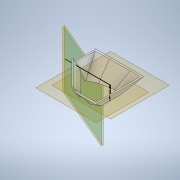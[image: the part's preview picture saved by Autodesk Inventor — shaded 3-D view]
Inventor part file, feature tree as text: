
AUTODESK INVENTOR PART (.ipt)
format: ipt  version: 2022 (Build 260153000, 153)  size: 218,112 bytes
history: native  units: in
note: dims shown in document units (in); Inventor stores cm internally (conversion verified against a paired STEP export)
features: plane x6, sketch x5, loft x1, shell x1, extrude x1, split x1
ambient origin geometry x8: Origin, YZ Plane, XZ Plane, XY Plane, X Axis, Y Axis, Z Axis, Center Point
bodies: Solid1 (feature_tree)
feature tree (15):
  sketch  "Sketch1"  dims[d0=0.1378in d1=0.2756in d2=0.1181in]
  sketch  "Sketch2"  dims[d3=120.0deg d4=0.962in]
  plane  "Work Plane8"
  plane  "Work Plane7"
  plane  "Work Plane9"
  sketch  "Sketch4"  dims[d5=0.2165in]
  plane  "Work Plane10"
  loft  "Loft1"
  shell  "Shell1"  Thickness=0.1181in
  plane  "Work Plane12"
  extrude  "Extrusion7"  Depth=0.962in
  sketch  "Sketch12"  dims[d9=0.1575in d10=0.1969in d23=0.3543in d24=0.7087in d25=0.7087in d52=0.0in d53=90.0deg d54=0.0in d55=90.0deg d56=0.0197in d63=0.1181in d64=0.1181in d65=0.0197in d66=0.0in d68=0.0197in d27=0.0197in d28=0.0344in d29=0.0197in d30=0.0344in d34=0.0197in d35=0.0344in d36=0.0197in d37=0.0344in]
  plane  "Work Plane14"
  split  "Split1"
  sketch  "Sketch11"  dims[d6=0.4528in]
